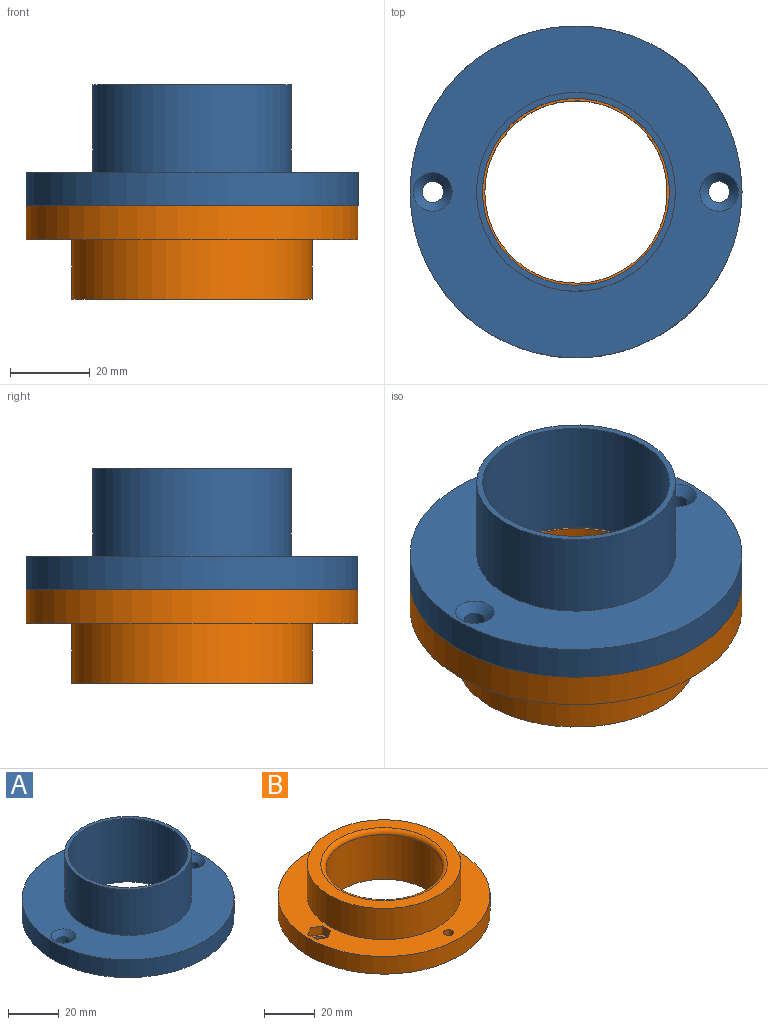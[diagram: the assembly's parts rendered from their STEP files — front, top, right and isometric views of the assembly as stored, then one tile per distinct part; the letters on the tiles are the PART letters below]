
ASSEMBLY  parts=2 mates=1
PART A: 10 faces, bbox 83.5x83.5x30.5 mm
  f0: cylinder r=41.75mm len=83.5mm, axis (0,0,1), area 2229.7mm2, adj f4,f5
  f1: cylinder r=2.65mm len=6.3mm, axis (0,0,1), area 104.9mm2, adj f4,f9
  f2: cylinder r=2.65mm len=6.3mm, axis (0,0,1), area 104.9mm2, adj f4,f8
  f3: cylinder r=23.5mm len=47mm, axis (0,0,1), area 4503.5mm2, adj f4,f7
  f4: plane 83.5x83.5mm, normal (0,0,-1), area 3696.9mm2, adj f0,f1,f2,f3
  f5: plane 83.5x83.5mm, normal (0,0,1), area 3364.7mm2, adj f0,f6,f8,f9
  f6: cylinder r=25mm len=50mm, axis (0,0,-1), area 3455.8mm2, adj f5,f7
  f7: plane 50x50mm, normal (0,0,1), area 228.6mm2, adj f3,f6
  f8: cone r=2.65mm half-angle=45deg, axis (0,0,1), area 73.3mm2, adj f2,f5
  f9: cone r=2.65mm half-angle=45deg, axis (0,0,1), area 73.3mm2, adj f1,f5
PART B: 29 faces, bbox 83.5x83.5x23.5 mm
  f0: cylinder r=4.25mm len=8.5mm, axis (0,0,1), area 80.1mm2, adj f6,f12
  f1: cylinder r=4.25mm len=8.5mm, axis (0,0,1), area 80.1mm2, adj f6,f11
  f2: cylinder r=22.93mm len=45.85mm, axis (0,0,-1), area 3096.9mm2, adj f6,f8
  f3: cylinder r=30.25mm len=60.5mm, axis (0,0,-1), area 2851mm2, adj f4,f7
  f4: plane 60.5x60.5mm, normal (0,0,1), area 923mm2, adj f3,f8
  f5: cylinder r=41.75mm len=83.5mm, axis (0,0,1), area 2229.7mm2, adj f6,f7
  f6: plane 83.5x83.5mm, normal (0,0,-1), area 3654.9mm2, adj f0,f1,f2,f5,f27,f28
  f7: plane 83.5x83.5mm, normal (0,0,1), area 2460.9mm2, adj f3,f5,f9,f10,f13,f14,f15,f16
  f8: torus R=24.93mm, axis (0,0,1), area 466.9mm2, adj f2,f4
  f9: cylinder r=1.95mm len=3.9mm, axis (0,0,-1), area 36.9mm2, adj f7,f11
  f10: cylinder r=1.95mm len=3.9mm, axis (0,0,-1), area 36.9mm2, adj f7,f12
  f11: torus R=4.45mm, axis (0,0,-1), area 65.1mm2, adj f1,f9
  f12: torus R=4.45mm, axis (0,0,-1), area 65.1mm2, adj f0,f10
  f13: plane 4.1x4mm, normal (-0.5,0.87,0), area 18.9mm2, adj f7,f14,f18,f19
  f14: plane 4.73x4mm, normal (-1,0,0), area 18.9mm2, adj f7,f13,f15,f19
  f15: plane 4.1x4mm, normal (-0.5,-0.87,0), area 18.9mm2, adj f7,f14,f16,f19
  f16: plane 4.1x4mm, normal (0.5,-0.87,0), area 18.9mm2, adj f7,f15,f17,f19
  f17: plane 4.73x4mm, normal (1,0,0), area 18.9mm2, adj f7,f16,f18,f19
  f18: plane 4.1x4mm, normal (0.5,0.87,0), area 18.9mm2, adj f7,f13,f17,f19
  f19: plane 9.47x8.2mm, normal (0,0,1), area 30mm2, adj f13,f14,f15,f16,f17,f18,f28
  f20: plane 4.1x4mm, normal (0.5,-0.87,0), area 18.9mm2, adj f7,f21,f25,f26
  f21: plane 4.73x4mm, normal (1,0,0), area 18.9mm2, adj f7,f20,f22,f26
  f22: plane 4.1x4mm, normal (0.5,0.87,0), area 18.9mm2, adj f7,f21,f23,f26
  f23: plane 4.1x4mm, normal (-0.5,0.87,0), area 18.9mm2, adj f7,f22,f24,f26
  f24: plane 4.73x4mm, normal (-1,0,0), area 18.9mm2, adj f7,f23,f25,f26
  f25: plane 4.1x4mm, normal (-0.5,-0.87,0), area 18.9mm2, adj f7,f20,f24,f26
  f26: plane 9.47x8.2mm, normal (0,0,1), area 30mm2, adj f20,f21,f22,f23,f24,f25,f27
  f27: cylinder r=3mm len=6mm, axis (0,0,1), area 84.8mm2, adj f6,f26
  f28: cylinder r=3mm len=6mm, axis (0,0,1), area 84.8mm2, adj f6,f19
PLACE A t=(-9.29,3.54,2.6)mm
PLACE B rot(axis=(0,1,0),180deg) t=(-9.29,3.54,-14.4)mm
MATE fastened B.f28 <-> A.f1  axis (0,0,1) through (-45.29,3.54,-5.9)mm
